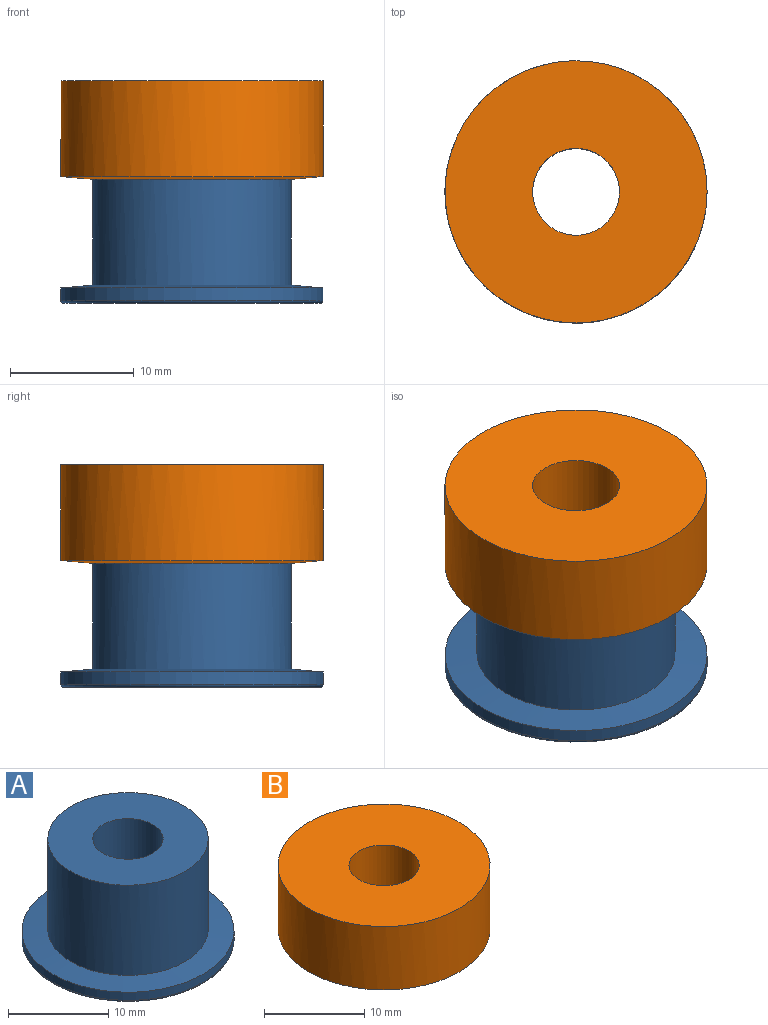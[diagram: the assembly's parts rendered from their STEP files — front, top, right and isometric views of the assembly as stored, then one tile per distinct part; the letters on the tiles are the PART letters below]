
ASSEMBLY  parts=2 mates=1
PART A: 7 faces, bbox 22.9x22.9x12.5 mm
  f0: cylinder r=8.01mm len=16.02mm, axis (0,0,1), area 554.8mm2, adj f4,f5
  f1: cylinder r=10.59mm len=21.17mm, axis (0,0,1), area 66.5mm2, adj f5,f6
  f2: plane 20.67x20.67mm, normal (0,0,-1), area 297mm2, adj f3,f6
  f3: cylinder r=3.51mm len=12.5mm, axis (0,0,1), area 275.5mm2, adj f2,f4
  f4: plane 16.02x16.02mm, normal (0,0,1), area 162.8mm2, adj f0,f3
  f5: cone r=7.73mm half-angle=85deg, axis (0,0,-1), area 151.2mm2, adj f0,f1
  f6: torus R=10.34mm, axis (0,0,-1), area 25.9mm2, adj f1,f2
PART B: 6 faces, bbox 21.2x21.2x8 mm
  f0: cylinder r=8.01mm len=16.02mm, axis (0,0,1), area 124.6mm2, adj f1,f5
  f1: plane 16.02x16.02mm, normal (0,0,-1), area 162.8mm2, adj f0,f2
  f2: cylinder r=3.51mm len=7.02mm, axis (0,0,1), area 121.2mm2, adj f1,f3
  f3: plane 21.17x21.17mm, normal (0,0,1), area 313.4mm2, adj f2,f4
  f4: cylinder r=10.59mm len=21.17mm, axis (0,0,1), area 515.5mm2, adj f3,f5
  f5: cone r=10.59mm half-angle=85deg, axis (0,0,1), area 151.2mm2, adj f0,f4
PLACE A at identity fixed
PLACE B at identity
MATE cylindrical A.f0 <-> B.f0  axis (0,0,1) through (0,0,12.5)mm
